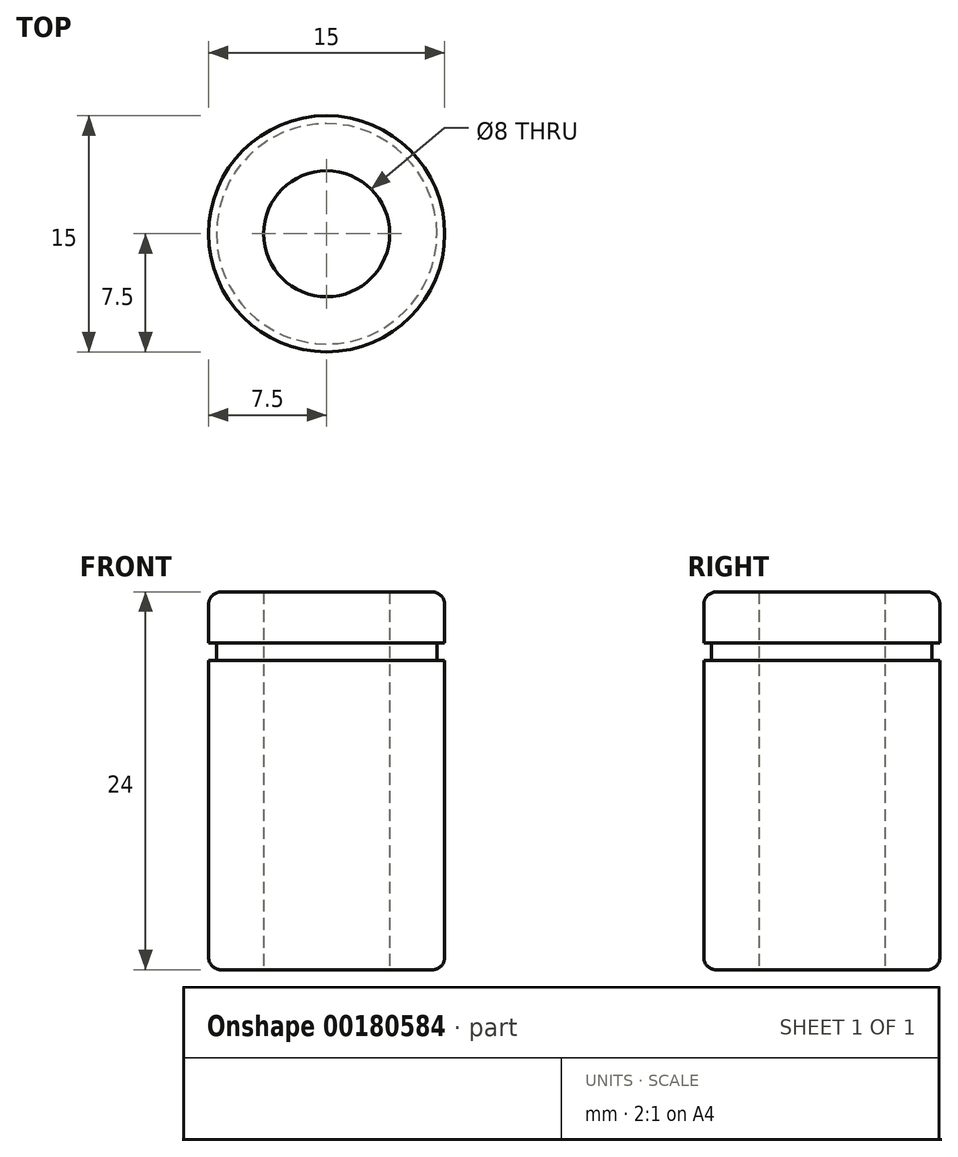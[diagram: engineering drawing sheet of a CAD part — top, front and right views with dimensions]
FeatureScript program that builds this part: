
annotation { "Feature Type Name" : "Feature", "Feature Type Description" : "" }
export const myFeature = defineFeature(function(context is Context, id is Id, definition is map)
    precondition{}
    {
        {
            var Q0;
            Q0=qCreatedBy(makeId("Top.planeOp"),FACE);
            var sketch = newSketch(context, id + "F0", { "sketchPlane" : qUnion([Q0])});
            skCircle(sketch, "E0", {"center": v(0, 0) * mm, "radius": 7.5 * mm});
            skCircle(sketch, "E1", {"center": v(0, 0) * mm, "radius": 4 * mm});
            skSolve(sketch);
        }
        {
            var Q0;
            Q0=makeQuery(id+"F0.imprint","IMPRINT",FACE,{"disambiguationData":[TD([[makeQuery(id+"F0.imprint","IMPRINT",EDGE,{"derivedFrom":sQuery(id+"F0.wireOp",EDGE,"E0")}),1.0]])]});
            extrude(context, id + "F1", {"entities" : qUnion([Q0]), "depth" : 24 * mm});
        }
        {
            var Q0;
            Q0=qCreatedBy(makeId("Front.planeOp"),FACE);
            var sketch = newSketch(context, id + "F2", { "sketchPlane" : qUnion([Q0])});
            skLineSegment(sketch, "E2.bottom", {"start": v(-7.5, 20.75) * mm, "end": v(-7, 20.75) * mm});
            skLineSegment(sketch, "E2.top", {"start": v(-7.5, 19.65) * mm, "end": v(-7, 19.65) * mm});
            skLineSegment(sketch, "E2.left", {"start": v(-7.5, 20.75) * mm, "end": v(-7.5, 19.65) * mm});
            skLineSegment(sketch, "E2.right", {"start": v(-7, 20.75) * mm, "end": v(-7, 19.65) * mm});
            skLineSegment(sketch, "E3", {"start": v(-7.5, 0) * mm, "end": v(-7.5, 24) * mm, "construction": true});
            skPoint(sketch, "E4", {"position": v(-7.5, 12) * mm});
            skLineSegment(sketch, "E5", {"start": v(-7.5, 12) * mm, "end": v(7.48, 12) * mm, "construction": true});
            skLineSegment(sketch, "E6.0", {"start": v(-7.5, 24) * mm, "end": v(7.5, 24) * mm, "construction": true});
            skLineSegment(sketch, "E7", {"start": v(-7.5, 0) * mm, "end": v(-7.5, 24) * mm});
            skLineSegment(sketch, "E8", {"start": v(7.5, 24) * mm, "end": v(7.5, 0) * mm});
            skLineSegment(sketch, "E9.MirrorCS", {"start": v(-7.5, 3.25) * mm, "end": v(-7.5, 4.35) * mm});
            skLineSegment(sketch, "E10.MirrorCS", {"start": v(-7, 3.25) * mm, "end": v(-7, 4.35) * mm});
            skLineSegment(sketch, "E11.MirrorCS", {"start": v(-7.5, 3.25) * mm, "end": v(-7, 3.25) * mm});
            skLineSegment(sketch, "E12.MirrorCS", {"start": v(-7.5, 4.35) * mm, "end": v(-7, 4.35) * mm});
            skLineSegment(sketch, "E13", {"start": v(0, 0) * mm, "end": v(0, 24) * mm, "construction": true});
            skSolve(sketch);
        }
        {
            var Q0;
            {var subQ0=sQuery(id+"F2.wireOp",EDGE,"E2.bottom");Q0=makeQuery(id+"F2.imprint","IMPRINT",FACE,{"disambiguationData":[TD([[makeQuery(id+"F2.imprint","IMPRINT",EDGE,{"derivedFrom":subQ0}),-1.0]])]});}
            var Q1;
            Q1=makeQuery(id+"F2.imprint","IMPRINT",FACE,{"disambiguationData":[TD([[makeQuery(id+"F2.imprint","IMPRINT",EDGE,{"derivedFrom":sQuery(id+"F2.wireOp",EDGE,"E9.MirrorCS")}),-1.0]])]});
            var Q2;
            Q2=sQuery(id+"F2.wireOp",EDGE,"E13");
            revolve(context, id + "F3", {"operationType" : NewBodyOperationType.REMOVE, "entities" : qUnion([Q0, Q1]), "axis" : qUnion([Q2]), "revolveType" : RevolveType.FULL, "oppositeDirection" : true});
        }
        {
            var Q0;
            Q0=makeQuery(id+"F1.opExtrude","CAP_EDGE",EDGE,{"disambiguationData":[OSD([sQuery(id+"F0.wireOp",EDGE,"E0")])],"isStart":false});
            var Q1;
            Q1=makeQuery(id+"F1.opExtrude","CAP_EDGE",EDGE,{"disambiguationData":[OSD([sQuery(id+"F0.wireOp",EDGE,"E0")])],"isStart":true});
            fillet(context, id + "F4", {"entities" : qUnion([Q0, Q1]), "radius" : 0.8 * mm, "tangentPropagation" : true, "allowEdgeOverflow" : false});
        }
    });
